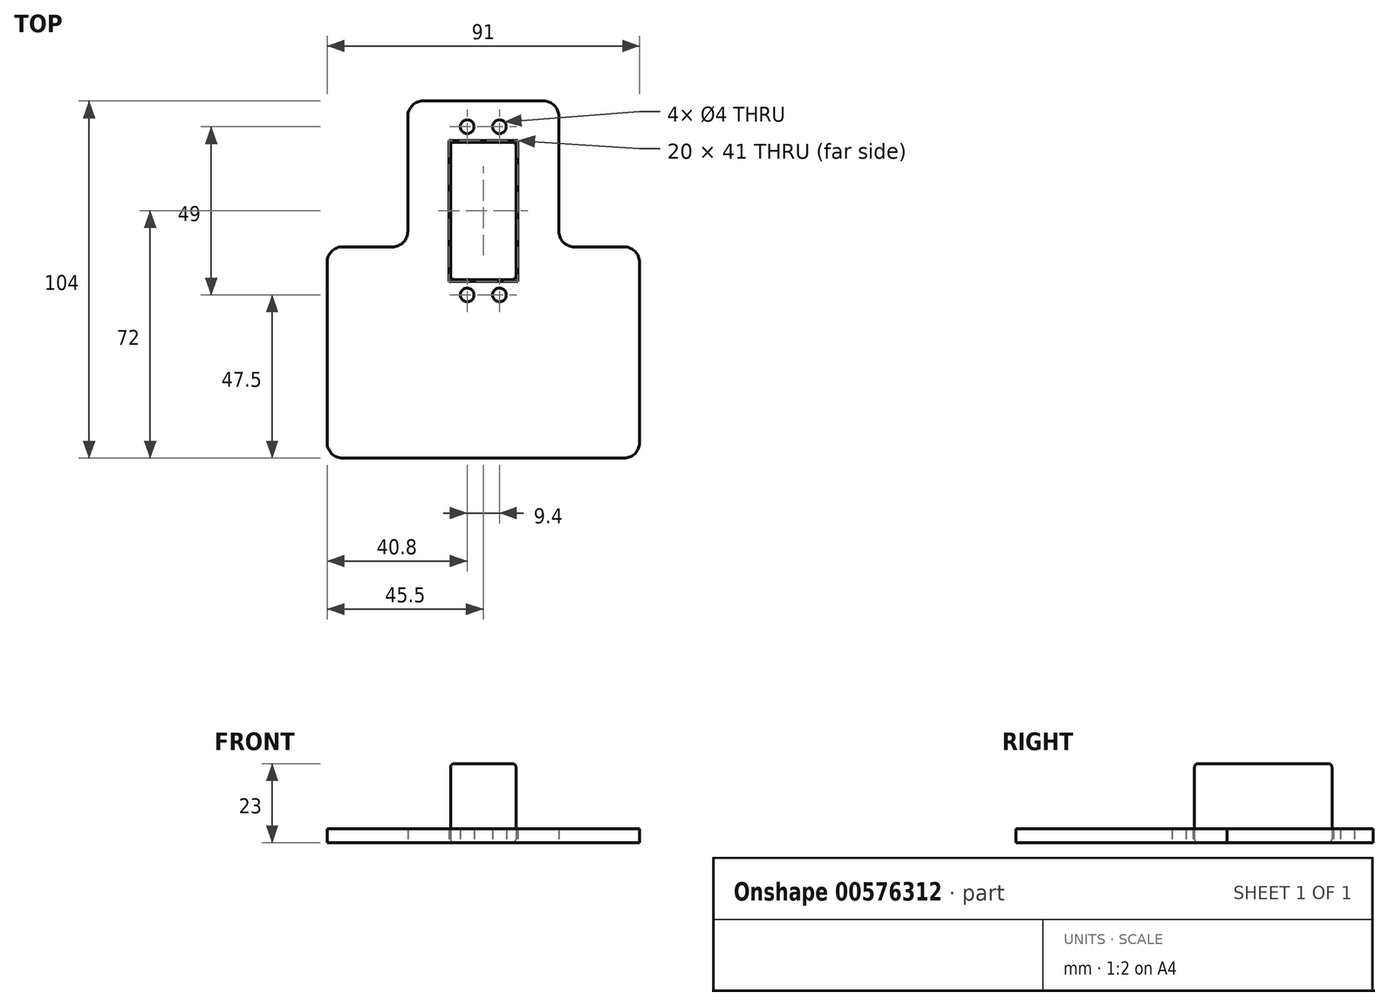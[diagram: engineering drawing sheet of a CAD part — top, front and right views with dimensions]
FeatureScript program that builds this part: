
annotation { "Feature Type Name" : "Feature", "Feature Type Description" : "" }
export const myFeature = defineFeature(function(context is Context, id is Id, definition is map)
    precondition{}
    {
        {
            var Q0;
            Q0=qCreatedBy(makeId("Top.planeOp"),FACE);
            var sketch = newSketch(context, id + "F0", { "sketchPlane" : qUnion([Q0])});
            skLineSegment(sketch, "E0.bottom", {"start": v(41, -30.75) * mm, "end": v(-41, -30.75) * mm});
            skLineSegment(sketch, "E0.top", {"start": v(41, 30.75) * mm, "end": v(26.5, 30.75) * mm});
            skLineSegment(sketch, "E0.left", {"start": v(45.5, -26.25) * mm, "end": v(45.5, 26.25) * mm});
            skLineSegment(sketch, "E0.right", {"start": v(-45.5, -26.25) * mm, "end": v(-45.5, 26.25) * mm});
            skPoint(sketch, "E0.middle", {"position": v(0, 0) * mm});
            skLineSegment(sketch, "E1.top", {"start": v(-17.5, 73.25) * mm, "end": v(17.5, 73.25) * mm});
            skLineSegment(sketch, "E1.left", {"start": v(-22, 35.25) * mm, "end": v(-22, 68.75) * mm});
            skLineSegment(sketch, "E1.right", {"start": v(22, 35.25) * mm, "end": v(22, 68.75) * mm});
            skLineSegment(sketch, "E2.bottom", {"start": v(-10, 61.75) * mm, "end": v(10, 61.75) * mm});
            skLineSegment(sketch, "E2.top", {"start": v(-10, 20.75) * mm, "end": v(10, 20.75) * mm});
            skLineSegment(sketch, "E2.left", {"start": v(-10, 61.75) * mm, "end": v(-10, 20.75) * mm});
            skLineSegment(sketch, "E2.right", {"start": v(10, 61.75) * mm, "end": v(10, 20.75) * mm});
            skCircle(sketch, "E3", {"center": v(4.7, 65.75) * mm, "radius": 2 * mm});
            skCircle(sketch, "E4", {"center": v(-4.7, 65.75) * mm, "radius": 2 * mm});
            skCircle(sketch, "E5", {"center": v(-4.7, 16.75) * mm, "radius": 2 * mm});
            skCircle(sketch, "E6", {"center": v(4.7, 16.75) * mm, "radius": 2 * mm});
            skLineSegment(sketch, "E7.trimOffspring", {"start": v(-26.5, 30.75) * mm, "end": v(-41, 30.75) * mm});
            skPoint(sketch, "E8.visualSharp", {"position": v(-45.5, 30.75) * mm});
            skArc(sketch, "E8.filletArc", {"start": v(-41, 30.75) * mm, "mid": v(-44.18, 29.43) * mm, "end": v(-45.5, 26.25) * mm});
            skPoint(sketch, "E9.visualSharp", {"position": v(-45.5, -30.75) * mm});
            skArc(sketch, "E9.filletArc", {"start": v(-45.5, -26.25) * mm, "mid": v(-44.18, -29.43) * mm, "end": v(-41, -30.75) * mm});
            skPoint(sketch, "E10.visualSharp", {"position": v(45.5, -30.75) * mm});
            skArc(sketch, "E10.filletArc", {"start": v(41, -30.75) * mm, "mid": v(44.18, -29.43) * mm, "end": v(45.5, -26.25) * mm});
            skPoint(sketch, "E11.visualSharp", {"position": v(45.5, 30.75) * mm});
            skArc(sketch, "E11.filletArc", {"start": v(45.5, 26.25) * mm, "mid": v(44.18, 29.43) * mm, "end": v(41, 30.75) * mm});
            skPoint(sketch, "E12.visualSharp", {"position": v(22, 30.75) * mm});
            skArc(sketch, "E12.filletArc", {"start": v(22, 35.25) * mm, "mid": v(23.32, 32.07) * mm, "end": v(26.5, 30.75) * mm});
            skPoint(sketch, "E13.visualSharp", {"position": v(-22, 30.75) * mm});
            skArc(sketch, "E13.filletArc", {"start": v(-26.5, 30.75) * mm, "mid": v(-23.32, 32.07) * mm, "end": v(-22, 35.25) * mm});
            skPoint(sketch, "E14.visualSharp", {"position": v(22, 73.25) * mm});
            skArc(sketch, "E14.filletArc", {"start": v(22, 68.75) * mm, "mid": v(20.68, 71.93) * mm, "end": v(17.5, 73.25) * mm});
            skPoint(sketch, "E15.visualSharp", {"position": v(-22, 73.25) * mm});
            skArc(sketch, "E15.filletArc", {"start": v(-17.5, 73.25) * mm, "mid": v(-20.68, 71.93) * mm, "end": v(-22, 68.75) * mm});
            skLineSegment(sketch, "E16", {"start": v(-10, 20.75) * mm, "end": v(-10, 13.22) * mm, "construction": true});
            skLineSegment(sketch, "E17", {"start": v(10, 20.75) * mm, "end": v(10, 12.95) * mm, "construction": true});
            skLineSegment(sketch, "E18", {"start": v(4.7, 16.75) * mm, "end": v(10, 16.75) * mm, "construction": true});
            skLineSegment(sketch, "E19", {"start": v(-4.7, 16.75) * mm, "end": v(-10, 16.75) * mm, "construction": true});
            skLineSegment(sketch, "E20", {"start": v(-10, 61.75) * mm, "end": v(-10, 69.3) * mm, "construction": true});
            skLineSegment(sketch, "E21", {"start": v(10, 61.75) * mm, "end": v(10, 68.87) * mm, "construction": true});
            skLineSegment(sketch, "E22", {"start": v(-4.7, 65.75) * mm, "end": v(-10, 65.75) * mm, "construction": true});
            skLineSegment(sketch, "E23", {"start": v(4.7, 65.75) * mm, "end": v(10, 65.75) * mm, "construction": true});
            skSolve(sketch);
        }
        {
            var Q0;
            Q0=makeQuery(id+"F0.imprint","IMPRINT",FACE,{"disambiguationData":[TD([[makeQuery(id+"F0.imprint","IMPRINT",EDGE,{"derivedFrom":sQuery(id+"F0.wireOp",EDGE,"E0.bottom")}),-1.0]])]});
            extrude(context, id + "F1", {"entities" : qUnion([Q0]), "depth" : 4 * mm, "offsetDistance" : 25 * mm});
        }
        {
            var Q0;
            Q0=qCreatedBy(makeId("Top.planeOp"),FACE);
            var sketch = newSketch(context, id + "F2", { "sketchPlane" : qUnion([Q0])});
            skLineSegment(sketch, "E24.bottom", {"start": v(-9.5, 61.25) * mm, "end": v(9.5, 61.25) * mm});
            skLineSegment(sketch, "E24.top", {"start": v(-9.5, 21.25) * mm, "end": v(9.5, 21.25) * mm});
            skLineSegment(sketch, "E24.left", {"start": v(-9.5, 61.25) * mm, "end": v(-9.5, 21.25) * mm});
            skLineSegment(sketch, "E24.right", {"start": v(9.5, 61.25) * mm, "end": v(9.5, 21.25) * mm});
            skSolve(sketch);
        }
        {
            var Q0;
            Q0=makeQuery(id+"F2.imprint","IMPRINT",FACE,{"disambiguationData":[TD([[makeQuery(id+"F2.imprint","IMPRINT",EDGE,{"derivedFrom":sQuery(id+"F2.wireOp",EDGE,"E24.bottom")}),-1.0]])]});
            extrude(context, id + "F3", {"entities" : qUnion([Q0]), "depth" : 23 * mm, "offsetDistance" : 25 * mm});
        }
        {
            var Q0;
            Q0=makeQuery(id+"F3.opExtrude","CAP_FACE",FACE,{"disambiguationData":[OSD([sQuery(id+"F2.wireOp",EDGE,"E24.bottom"),sQuery(id+"F2.wireOp",EDGE,"E24.top"),sQuery(id+"F2.wireOp",EDGE,"E24.left"),sQuery(id+"F2.wireOp",EDGE,"E24.right")])],"isStart":false});
            var Q1;
            Q1=makeQuery(id+"F3.opExtrude","SWEPT_FACE",FACE,{"disambiguationData":[OSD([sQuery(id+"F2.wireOp",EDGE,"E24.top")])]});
            var Q2;
            Q2=makeQuery(id+"F3.opExtrude","SWEPT_FACE",FACE,{"disambiguationData":[OSD([sQuery(id+"F2.wireOp",EDGE,"E24.right")])]});
            var Q3;
            Q3=makeQuery(id+"F3.opExtrude","SWEPT_FACE",FACE,{"disambiguationData":[OSD([sQuery(id+"F2.wireOp",EDGE,"E24.bottom")])]});
            var Q4;
            Q4=makeQuery(id+"F3.opExtrude","SWEPT_FACE",FACE,{"disambiguationData":[OSD([sQuery(id+"F2.wireOp",EDGE,"E24.left")])]});
            fillet(context, id + "F4", {"entities" : qUnion([Q0, Q1, Q2, Q3, Q4]), "radius" : 1 * mm, "tangentPropagation" : true, "allowEdgeOverflow" : false});
        }
    });
